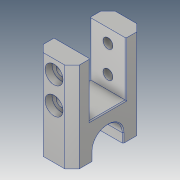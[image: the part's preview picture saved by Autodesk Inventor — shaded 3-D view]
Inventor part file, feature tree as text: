
AUTODESK INVENTOR PART (.ipt)
format: ipt  version: 2018.2 (Build 222227000, 227)  size: 207,360 bytes
history: native  units: mm
features: sketch x5, extrude x2, hole x2, projected_geometry x2, mirror x1, chamfer x1
ambient origin geometry x8: Origin, YZ Plane, XZ Plane, XY Plane, X Axis, Y Axis, Z Axis, Center Point
bodies: Volumenkörper1 (feature_tree)
feature tree (13):
  extrude  "Grundkörper"  Depth=50.0mm
  extrude  "Ausschnitt"  Depth=30.0mm
  hole  "DIN7984_M5_Boh"  [1 undecoded]
  mirror  "Spiegeln_DIN7984_M5_Boh"
  hole  "M5x10"  [1 undecoded]
  sketch  "Skizze"  dims[d19=30.0mm d20=15.0mm d21=15.0mm d22=5.5mm d23=6.0mm d24=10.0mm d25=3.9mm d26=90.0deg d27=8.0mm d28=20.594885mm d29=28.4mm d30=4.134mm d31=10.0mm d32=5.0mm d33=3.9mm d34=90.0deg d35=14.2mm d36=20.594885mm d37=4.0mm d38=2.0mm d39=45.0deg d40=0.5mm d41=2.0mm d42=45.0deg]
  chamfer  "Fase_Allgemein"  Distance=40.0mm
  sketch  "Skizze1"  dims[d0=40.0mm d1=50.0mm]
  sketch  "Skizze2"  dims[d2=20.0mm d3=0.0mm d4=30.0mm]
  sketch  "Skizze4"  dims[d5=20.0mm d14=13.0mm]
  sketch  "Skizze5"  dims[d15=16.8mm d16=8.0mm d17=40.0mm d18=0.0mm]
  projected_geometry  "Projizierte Kontur1"
  projected_geometry  "Projizierte Kontur2"
note: 2 required parameter values undecoded (feature->parameter linkage not recoverable at this tier; creation-order binding heuristic only, values carry confidence <= 0.55)
